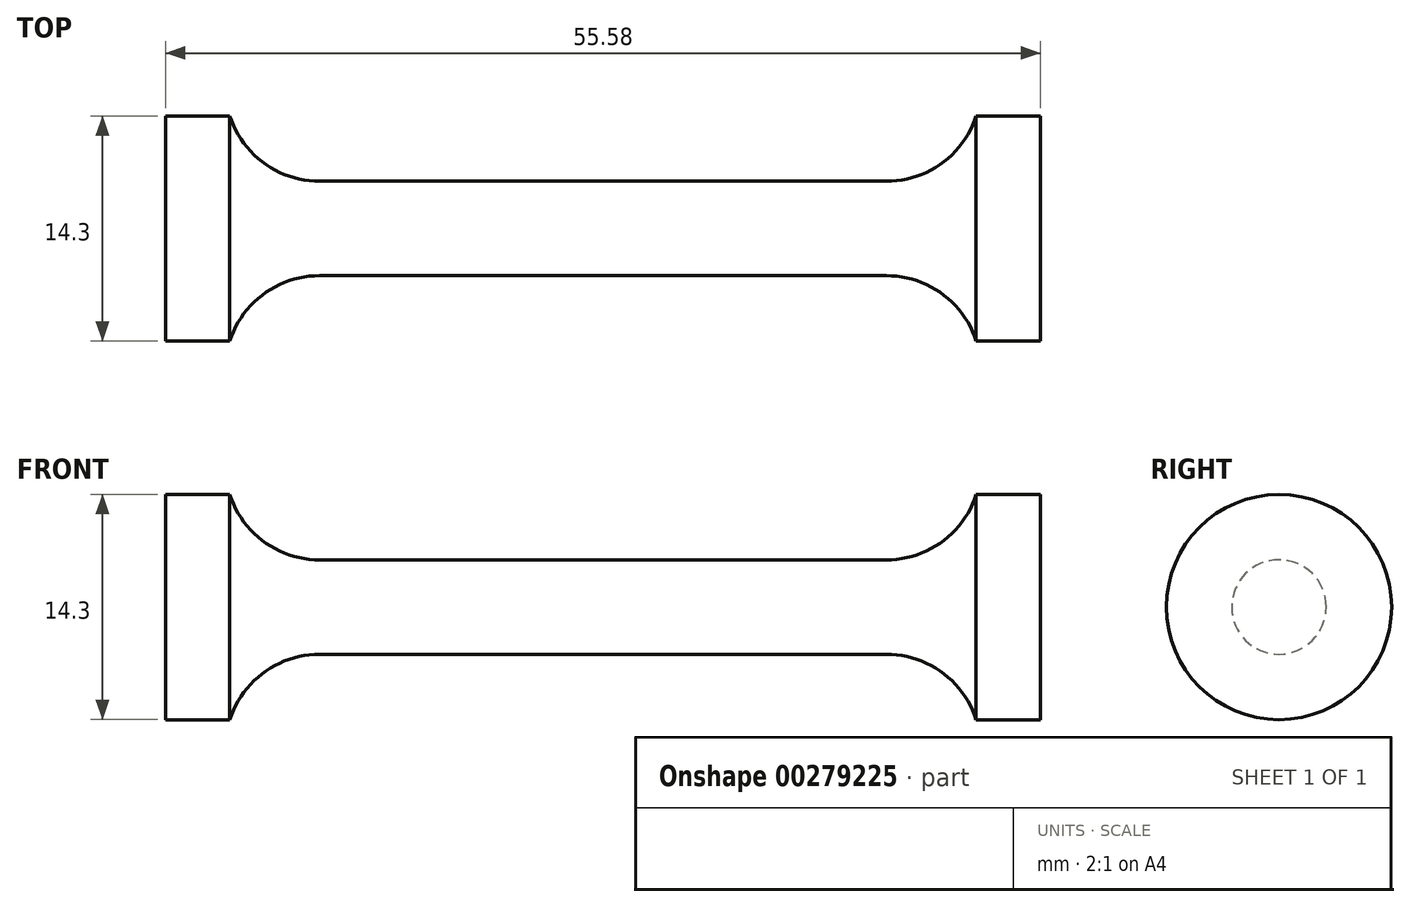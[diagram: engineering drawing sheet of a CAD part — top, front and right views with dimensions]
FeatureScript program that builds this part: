
annotation { "Feature Type Name" : "Feature", "Feature Type Description" : "" }
export const myFeature = defineFeature(function(context is Context, id is Id, definition is map)
    precondition{}
    {
        {
            var Q0;
            Q0=qCreatedBy(makeId("Front.planeOp"),FACE);
            var sketch = newSketch(context, id + "F0", { "sketchPlane" : qUnion([Q0])});
            skLineSegment(sketch, "E0", {"start": v(0, 3) * mm, "end": v(18, 3) * mm});
            skArc(sketch, "E1", {"start": v(18, 3) * mm, "mid": v(21.53, 4.15) * mm, "end": v(23.7, 7.15) * mm});
            skLineSegment(sketch, "E2", {"start": v(23.7, 7.15) * mm, "end": v(27.8, 7.15) * mm});
            skLineSegment(sketch, "E3", {"start": v(27.8, 7.15) * mm, "end": v(27.8, 0) * mm});
            skLineSegment(sketch, "E4.MirrorCS", {"start": v(0, 3) * mm, "end": v(-18, 3) * mm});
            skLineSegment(sketch, "E5.MirrorCS", {"start": v(-27.8, 7.15) * mm, "end": v(-27.8, 0) * mm});
            skLineSegment(sketch, "E6.MirrorCS", {"start": v(-23.7, 7.15) * mm, "end": v(-27.8, 7.15) * mm});
            skArc(sketch, "E7.MirrorCS", {"start": v(-18, 3) * mm, "mid": v(-21.53, 4.15) * mm, "end": v(-23.7, 7.15) * mm});
            skLineSegment(sketch, "E8", {"start": v(-27.8, 0) * mm, "end": v(27.8, 0) * mm});
            skSolve(sketch);
        }
        {
            var Q0;
            Q0 = qSketchRegion(id + "F0", true);
            var Q1;
            Q1=sQuery(id+"F0.wireOp",EDGE,"E8");
            revolve(context, id + "F1", {"entities" : qUnion([Q0]), "axis" : qUnion([Q1]), "revolveType" : RevolveType.FULL});
        }
    });
